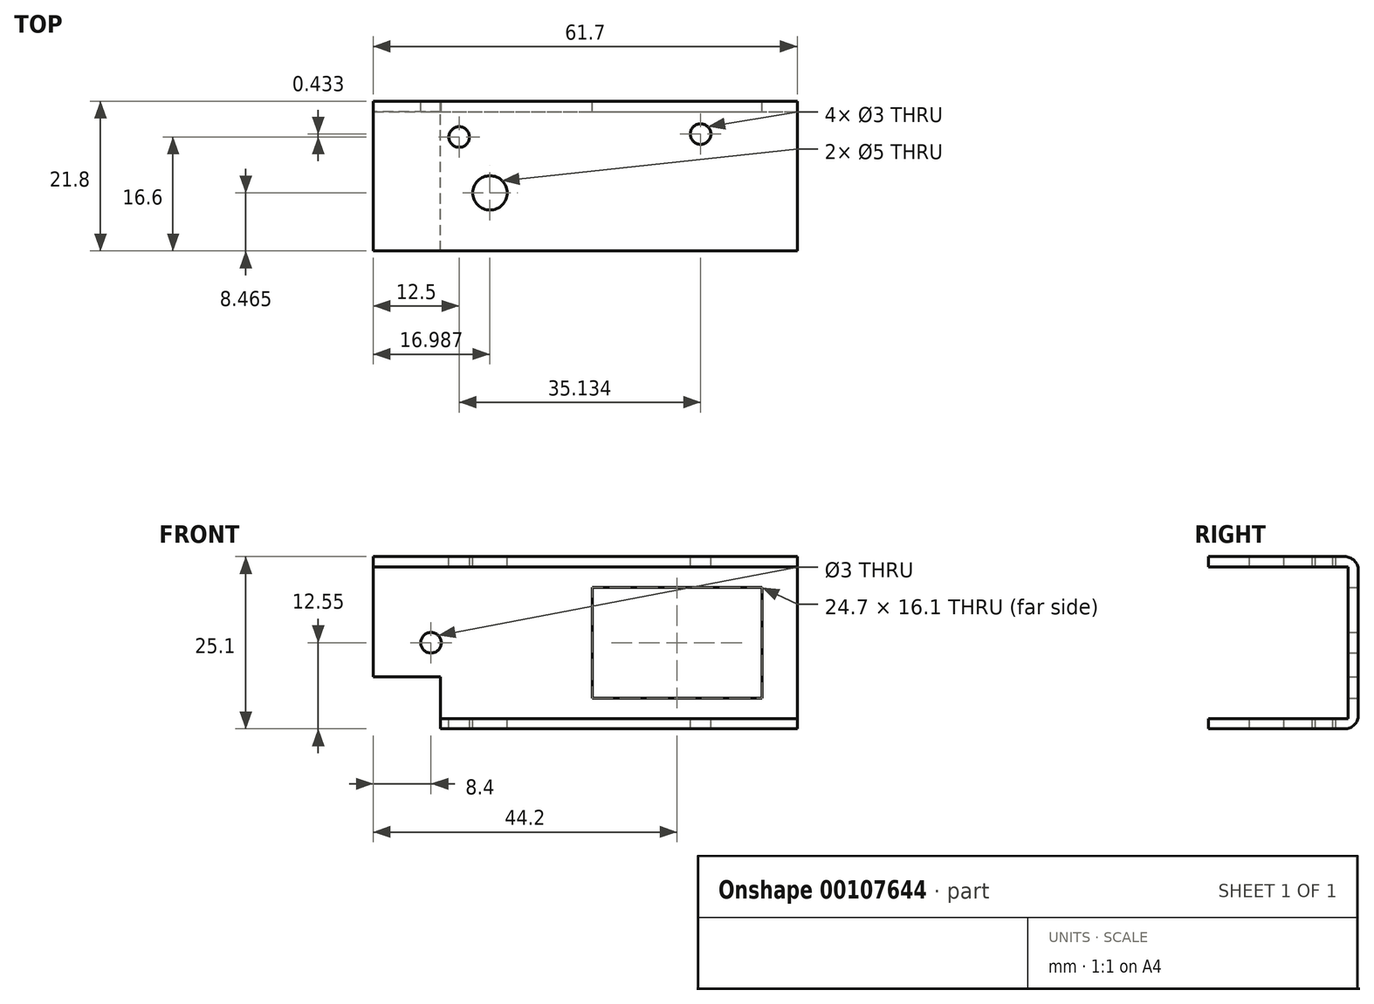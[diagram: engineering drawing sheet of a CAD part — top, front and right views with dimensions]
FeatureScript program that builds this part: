
annotation { "Feature Type Name" : "Feature", "Feature Type Description" : "" }
export const myFeature = defineFeature(function(context is Context, id is Id, definition is map)
    precondition{}
    {
        {
            var Q0;
            Q0=qCreatedBy(makeId("Front.planeOp"),FACE);
            var sketch = newSketch(context, id + "F0", { "sketchPlane" : qUnion([Q0])});
            skLineSegment(sketch, "E0.bottom", {"start": v(-30.85, 12.55) * mm, "end": v(30.85, 12.55) * mm});
            skLineSegment(sketch, "E0.top", {"start": v(-21.05, -12.55) * mm, "end": v(30.85, -12.55) * mm});
            skLineSegment(sketch, "E0.left", {"start": v(-30.85, 12.55) * mm, "end": v(-30.85, 11.05) * mm});
            skLineSegment(sketch, "E0.right", {"start": v(30.85, 12.55) * mm, "end": v(30.85, 11.05) * mm});
            skPoint(sketch, "E0.middle", {"position": v(0, 0) * mm});
            skLineSegment(sketch, "E1", {"start": v(-21.05, -11.05) * mm, "end": v(30.85, -11.05) * mm});
            skLineSegment(sketch, "E2", {"start": v(-30.85, 11.05) * mm, "end": v(30.85, 11.05) * mm});
            skLineSegment(sketch, "E3", {"start": v(1, 8.05) * mm, "end": v(25.7, 8.05) * mm});
            skLineSegment(sketch, "E4", {"start": v(1, -8.05) * mm, "end": v(25.7, -8.05) * mm});
            skLineSegment(sketch, "E5", {"start": v(1, 8.05) * mm, "end": v(1, -8.05) * mm});
            skLineSegment(sketch, "E6.trimOffspring", {"start": v(25.7, 8.05) * mm, "end": v(25.7, -8.05) * mm});
            skCircle(sketch, "E7", {"center": v(-22.45, 0) * mm, "radius": 1.5 * mm});
            skLineSegment(sketch, "E8", {"start": v(-30.85, 11.05) * mm, "end": v(-30.85, -4.95) * mm});
            skLineSegment(sketch, "E9", {"start": v(30.85, 11.05) * mm, "end": v(30.85, 11.05) * mm});
            skLineSegment(sketch, "E10", {"start": v(30.85, -11.05) * mm, "end": v(30.85, -11.05) * mm});
            skLineSegment(sketch, "E11", {"start": v(30.85, -11.05) * mm, "end": v(30.85, -12.55) * mm});
            skLineSegment(sketch, "E12", {"start": v(30.85, 11.05) * mm, "end": v(30.85, -11.05) * mm});
            skLineSegment(sketch, "E13", {"start": v(-21.05, -11.05) * mm, "end": v(-21.05, -12.55) * mm});
            skLineSegment(sketch, "E14", {"start": v(-21.05, -11.05) * mm, "end": v(-21.05, 10.13) * mm});
            skLineSegment(sketch, "E15", {"start": v(-21.05, -4.95) * mm, "end": v(-32.07, -4.95) * mm});
            skSolve(sketch);
        }
        {
            var Q0;
            Q0=makeQuery(id+"F0.imprint","IMPRINT",FACE,{"disambiguationData":[TD([[makeQuery(id+"F0.imprint","IMPRINT",EDGE,{"derivedFrom":sQuery(id+"F0.wireOp",EDGE,"E1")}),1.0]])]});
            extrude(context, id + "F1", {"entities" : qUnion([Q0]), "depth" : 1.5 * mm});
        }
        {
            var Q0;
            Q0=makeQuery(id+"F0.imprint","IMPRINT",FACE,{"disambiguationData":[TD([[makeQuery(id+"F0.imprint","IMPRINT",EDGE,{"derivedFrom":sQuery(id+"F0.wireOp",EDGE,"E0.top")}),1.0]])]});
            extrude(context, id + "F2", {"entities" : qUnion([Q0]), "operationType" : NewBodyOperationType.ADD, "depth" : 21.8 * mm});
        }
        {
            var Q0;
            Q0=makeQuery(id+"F0.imprint","IMPRINT",FACE,{"disambiguationData":[TD([[makeQuery(id+"F0.imprint","IMPRINT",EDGE,{"derivedFrom":sQuery(id+"F0.wireOp",EDGE,"E0.bottom")}),-1.0]])]});
            extrude(context, id + "F3", {"entities" : qUnion([Q0]), "operationType" : NewBodyOperationType.ADD, "depth" : 21.8 * mm});
        }
        {
            var Q0;
            Q0=makeQuery(id+"F3.opExtrude","CAP_EDGE",EDGE,{"disambiguationData":[OSD([sQuery(id+"F0.wireOp",EDGE,"E0.bottom")])],"isStart":true});
            var Q1;
            Q1=makeQuery(id+"F2.opExtrude","CAP_EDGE",EDGE,{"disambiguationData":[OSD([sQuery(id+"F0.wireOp",EDGE,"E0.top")])],"isStart":true});
            fillet(context, id + "F4", {"entities" : qUnion([Q0, Q1]), "radius" : 2 * mm, "tangentPropagation" : true, "allowEdgeOverflow" : false});
        }
        {
            var Q0;
            Q0=makeQuery(id+"F3.opExtrude","SWEPT_FACE",FACE,{"disambiguationData":[OSD([sQuery(id+"F0.wireOp",EDGE,"E0.bottom")])]});
            var sketch = newSketch(context, id + "F5", { "sketchPlane" : qUnion([Q0])});
            skCircle(sketch, "E16", {"center": v(-13.86, -13.33) * mm, "radius": 2.75 * mm});
            skCircle(sketch, "E17", {"center": v(16.78, -4.77) * mm, "radius": 1.65 * mm});
            skLineSegment(sketch, "E18", {"start": v(-17.85, -5.2) * mm, "end": v(-17.85, -25.11) * mm});
            skLineSegment(sketch, "E19", {"start": v(-13.86, -13.33) * mm, "end": v(-13.86, -26.92) * mm});
            skLineSegment(sketch, "E20", {"start": v(-17.85, -5.2) * mm, "end": v(-7.7, -5.2) * mm});
            skLineSegment(sketch, "E21", {"start": v(-13.86, -13.33) * mm, "end": v(-2.44, -13.33) * mm});
            skLineSegment(sketch, "E22", {"start": v(-17.85, -5.2) * mm, "end": v(-18.35, -5.2) * mm});
            skCircle(sketch, "E23", {"center": v(-18.35, -5.2) * mm, "radius": 1.5 * mm});
            skLineSegment(sketch, "E24", {"start": v(-16.16, -5.2) * mm, "end": v(22.3, -5.2) * mm});
            skSolve(sketch);
        }
        {
            var Q0;
            Q0=sQuery(id+"F5.wireOp",VERTEX,"E16.center");
            var Q1;
            Q1=makeQuery(id+"F1.opExtrude","SWEPT_BODY",BODY,{"disambiguationData":[OSD([sQuery(id+"F0.wireOp",EDGE,"E1"),sQuery(id+"F0.wireOp",EDGE,"E2"),sQuery(id+"F0.wireOp",EDGE,"E3"),sQuery(id+"F0.wireOp",EDGE,"E4"),sQuery(id+"F0.wireOp",EDGE,"E5"),sQuery(id+"F0.wireOp",EDGE,"E6.trimOffspring"),sQuery(id+"F0.wireOp",EDGE,"E7"),sQuery(id+"F0.wireOp",EDGE,"E8"),sQuery(id+"F0.wireOp",EDGE,"E12")])]});
            hole(context, id + "F6", {"style" : HoleStyle.SIMPLE, "endStyle" : HoleEndStyle.BLIND, "holeDiameter" : 5 * mm, "holeDepth" : 100 * mm, "startFromSketch" : true, "locations" : qUnion([Q0]), "scope" : qUnion([Q1])});
        }
        {
            var Q0;
            Q0=sQuery(id+"F5.wireOp",VERTEX,"E17.center");
            var Q1;
            Q1=makeQuery(id+"F1.opExtrude","SWEPT_BODY",BODY,{"disambiguationData":[OSD([sQuery(id+"F0.wireOp",EDGE,"E1"),sQuery(id+"F0.wireOp",EDGE,"E2"),sQuery(id+"F0.wireOp",EDGE,"E3"),sQuery(id+"F0.wireOp",EDGE,"E4"),sQuery(id+"F0.wireOp",EDGE,"E5"),sQuery(id+"F0.wireOp",EDGE,"E6.trimOffspring"),sQuery(id+"F0.wireOp",EDGE,"E7"),sQuery(id+"F0.wireOp",EDGE,"E8"),sQuery(id+"F0.wireOp",EDGE,"E12")])]});
            hole(context, id + "F7", {"style" : HoleStyle.SIMPLE, "endStyle" : HoleEndStyle.BLIND, "holeDiameter" : 3 * mm, "holeDepth" : 100 * mm, "startFromSketch" : true, "locations" : qUnion([Q0]), "scope" : qUnion([Q1])});
        }
        {
            var Q0;
            Q0=sQuery(id+"F5.wireOp",VERTEX,"E22.end");
            var Q1;
            Q1=makeQuery(id+"F1.opExtrude","SWEPT_BODY",BODY,{"disambiguationData":[OSD([sQuery(id+"F0.wireOp",EDGE,"E1"),sQuery(id+"F0.wireOp",EDGE,"E2"),sQuery(id+"F0.wireOp",EDGE,"E3"),sQuery(id+"F0.wireOp",EDGE,"E4"),sQuery(id+"F0.wireOp",EDGE,"E5"),sQuery(id+"F0.wireOp",EDGE,"E6.trimOffspring"),sQuery(id+"F0.wireOp",EDGE,"E7"),sQuery(id+"F0.wireOp",EDGE,"E8"),sQuery(id+"F0.wireOp",EDGE,"E12"),sQuery(id+"F0.wireOp",EDGE,"E14"),sQuery(id+"F0.wireOp",EDGE,"E15")])]});
            hole(context, id + "F8", {"style" : HoleStyle.SIMPLE, "endStyle" : HoleEndStyle.THROUGH, "holeDiameter" : 3 * mm, "startFromSketch" : true, "locations" : qUnion([Q0]), "scope" : qUnion([Q1]), "isTappedThrough" : true});
        }
    });
